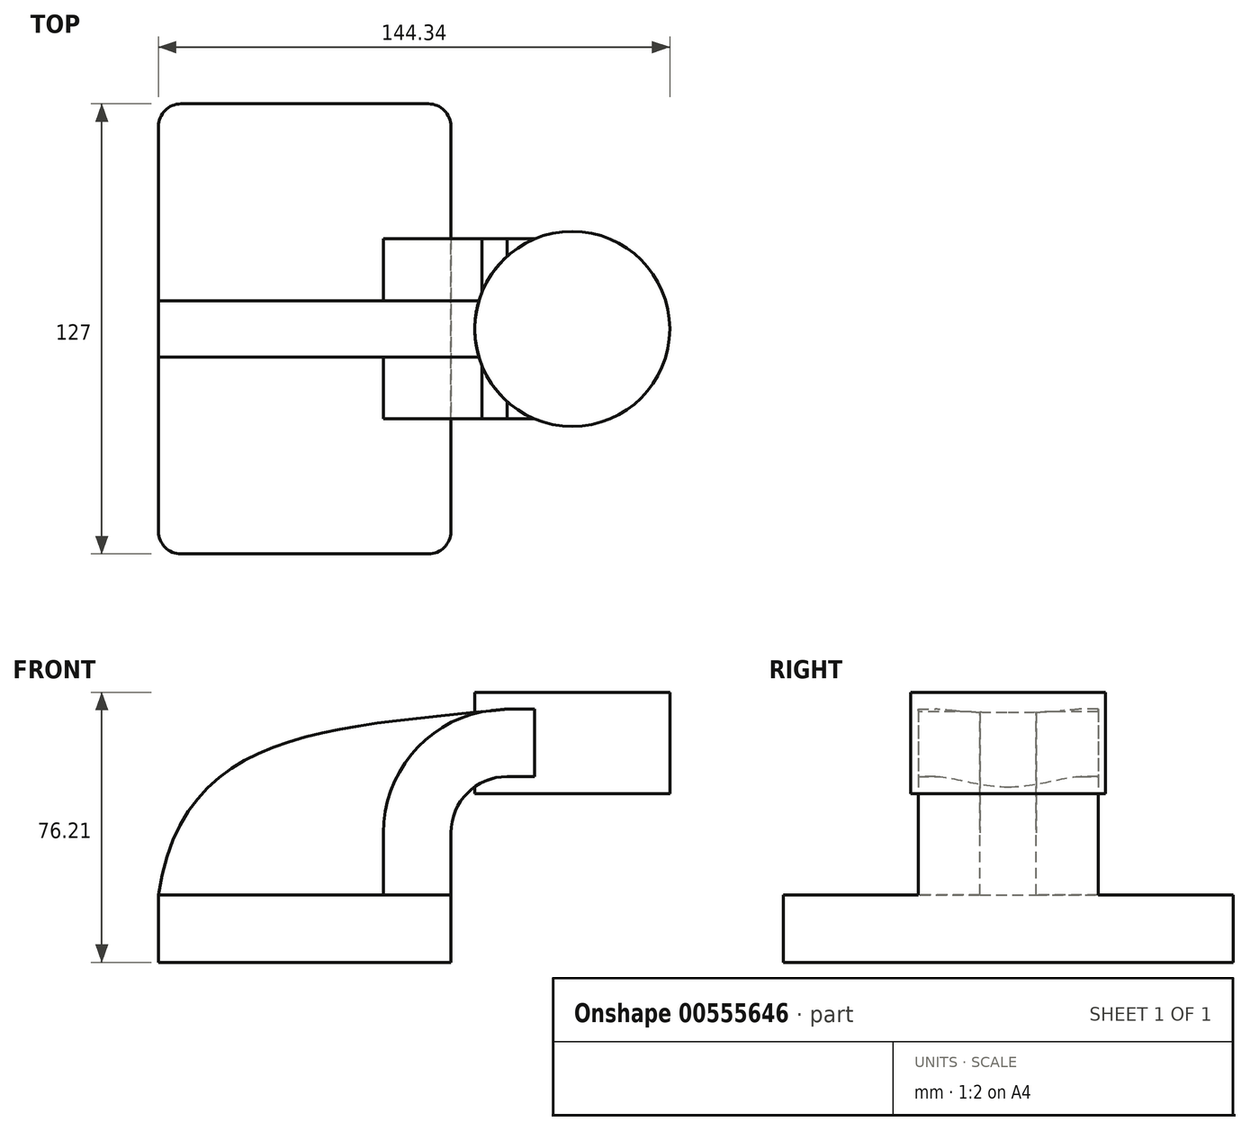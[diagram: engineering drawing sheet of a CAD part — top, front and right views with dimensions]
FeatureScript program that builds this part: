
annotation { "Feature Type Name" : "Feature", "Feature Type Description" : "" }
export const myFeature = defineFeature(function(context is Context, id is Id, definition is map)
    precondition{}
    {
        {
            var Q0;
            Q0=qCreatedBy(makeId("Front.planeOp"),FACE);
            var sketch = newSketch(context, id + "F0", { "sketchPlane" : qUnion([Q0])});
            skLineSegment(sketch, "E0.bottom", {"start": v(-41.28, 9.52) * mm, "end": v(41.27, 9.53) * mm});
            skLineSegment(sketch, "E0.top", {"start": v(-41.28, -9.53) * mm, "end": v(41.28, -9.53) * mm});
            skLineSegment(sketch, "E0.left", {"start": v(-41.28, 9.52) * mm, "end": v(-41.27, -9.53) * mm});
            skLineSegment(sketch, "E0.right", {"start": v(41.28, 9.53) * mm, "end": v(41.28, -9.52) * mm});
            skPoint(sketch, "E0.middle", {"position": v(0, 0) * mm});
            skLineSegment(sketch, "E1.bottom", {"start": v(52.26, 66.67) * mm, "end": v(103.06, 66.67) * mm});
            skLineSegment(sketch, "E1.top", {"start": v(52.26, 38.1) * mm, "end": v(103.06, 38.1) * mm});
            skLineSegment(sketch, "E1.left", {"start": v(52.26, 66.67) * mm, "end": v(52.26, 38.1) * mm});
            skLineSegment(sketch, "E1.right", {"start": v(103.06, 66.67) * mm, "end": v(103.06, 38.1) * mm});
            skPoint(sketch, "E1.middle", {"position": v(77.66, 52.39) * mm});
            skLineSegment(sketch, "E2", {"start": v(41.27, 9.53) * mm, "end": v(41.27, 27) * mm});
            skArc(sketch, "E3", {"start": v(41.27, 27) * mm, "mid": v(45.92, 38.23) * mm, "end": v(57.15, 42.88) * mm});
            skLineSegment(sketch, "E4", {"start": v(57.15, 42.88) * mm, "end": v(75.54, 42.88) * mm});
            skLineSegment(sketch, "E5.1", {"start": v(238.13, 9.53) * mm, "end": v(238.13, 138.8) * mm});
            skLineSegment(sketch, "E6.0", {"start": v(57.15, 61.93) * mm, "end": v(75.54, 61.93) * mm});
            skArc(sketch, "E6.1", {"start": v(22.22, 27) * mm, "mid": v(32.45, 51.7) * mm, "end": v(57.15, 61.93) * mm});
            skLineSegment(sketch, "E6.2", {"start": v(22.23, 9.53) * mm, "end": v(22.23, 27) * mm});
            skLineSegment(sketch, "E7", {"start": v(75.54, 38.1) * mm, "end": v(75.54, 66.67) * mm});
            skPoint(sketch, "E7.startSnap0", {"position": v(77.66, 38.1) * mm});
            skPoint(sketch, "E7.endSnap0", {"position": v(77.66, 66.67) * mm});
            skFitSpline(sketch, "E8", {"points": [v(-41.28, 9.53) * mm, v(57.15, 61.93) * mm], "startDerivative": vector(20.04, 141.3) * mm, "endDerivative": vector(149.25, 15.9) * mm});
            skSolve(sketch);
        }
        {
            var Q0;
            Q0=makeQuery(id+"F0.imprint","IMPRINT",FACE,{"disambiguationData":[TD([[makeQuery(id+"F0.imprint","IMPRINT",EDGE,{"derivedFrom":sQuery(id+"F0.wireOp",EDGE,"E0.top")}),1.0]])]});
            extrude(context, id + "F1", {"entities" : qUnion([Q0]), "endBound" : BoundingType.SYMMETRIC, "depth" : 127 * mm, "offsetDistance" : 25.4 * mm});
        }
        {
            var Q0;
            {var subQ1=sQuery(id+"F0.wireOp",EDGE,"E2");Q0=makeQuery(id+"F0.imprint","IMPRINT",FACE,{"disambiguationData":[TD([[makeQuery(id+"F0.imprint","IMPRINT",EDGE,{"derivedFrom":subQ1}),1.0]])]});}
            var Q1;
            {var subQ1=sQuery(id+"F0.wireOp",EDGE,"E4");Q1=makeQuery(id+"F0.imprint","IMPRINT",FACE,{"disambiguationData":[TD([[makeQuery(id+"F0.imprint","IMPRINT",EDGE,{"derivedFrom":subQ1}),1.0]])]});}
            extrude(context, id + "F2", {"entities" : qUnion([Q0, Q1]), "operationType" : NewBodyOperationType.ADD, "endBound" : BoundingType.SYMMETRIC, "oppositeDirection" : true, "depth" : 50.8 * mm, "offsetDistance" : 25.4 * mm});
        }
        {
            var Q0;
            {var subQ3=sQuery(id+"F0.wireOp",EDGE,"E6.2");Q0=makeQuery(id+"F0.imprint","IMPRINT",FACE,{"disambiguationData":[TD([[makeQuery(id+"F0.imprint","IMPRINT",EDGE,{"derivedFrom":subQ3}),1.0]])]});}
            extrude(context, id + "F3", {"entities" : qUnion([Q0]), "operationType" : NewBodyOperationType.ADD, "endBound" : BoundingType.SYMMETRIC, "depth" : 15.88 * mm, "offsetDistance" : 25.4 * mm});
        }
        {
            var Q0;
            {var subQ4=sQuery(id+"F0.wireOp",EDGE,"E1.right");Q0=makeQuery(id+"F0.imprint","IMPRINT",FACE,{"disambiguationData":[TD([[makeQuery(id+"F0.imprint","IMPRINT",EDGE,{"derivedFrom":subQ4}),-1.0]])]});}
            var Q1;
            Q1=sQuery(id+"F0.wireOp",EDGE,"E7");
            revolve(context, id + "F4", {"operationType" : NewBodyOperationType.ADD, "entities" : qUnion([Q0]), "axis" : qUnion([Q1]), "revolveType" : RevolveType.FULL});
        }
        {
            var Q0;
            Q0=makeQuery(id+"F1.opExtrude","CAP_EDGE",EDGE,{"disambiguationData":[OSD([sQuery(id+"F0.wireOp",EDGE,"E0.right")])],"isStart":false});
            var Q1;
            Q1=makeQuery(id+"F1.opExtrude","CAP_EDGE",EDGE,{"disambiguationData":[OSD([sQuery(id+"F0.wireOp",EDGE,"E0.left")])],"isStart":false});
            var Q2;
            Q2=makeQuery(id+"F1.opExtrude","CAP_EDGE",EDGE,{"disambiguationData":[OSD([sQuery(id+"F0.wireOp",EDGE,"E0.right")])],"isStart":true});
            var Q3;
            Q3=makeQuery(id+"F1.opExtrude","CAP_EDGE",EDGE,{"disambiguationData":[OSD([sQuery(id+"F0.wireOp",EDGE,"E0.left")])],"isStart":true});
            fillet(context, id + "F5", {"entities" : qUnion([Q0, Q1, Q2, Q3]), "radius" : 6.35 * mm, "tangentPropagation" : true, "allowEdgeOverflow" : false});
        }
    });
